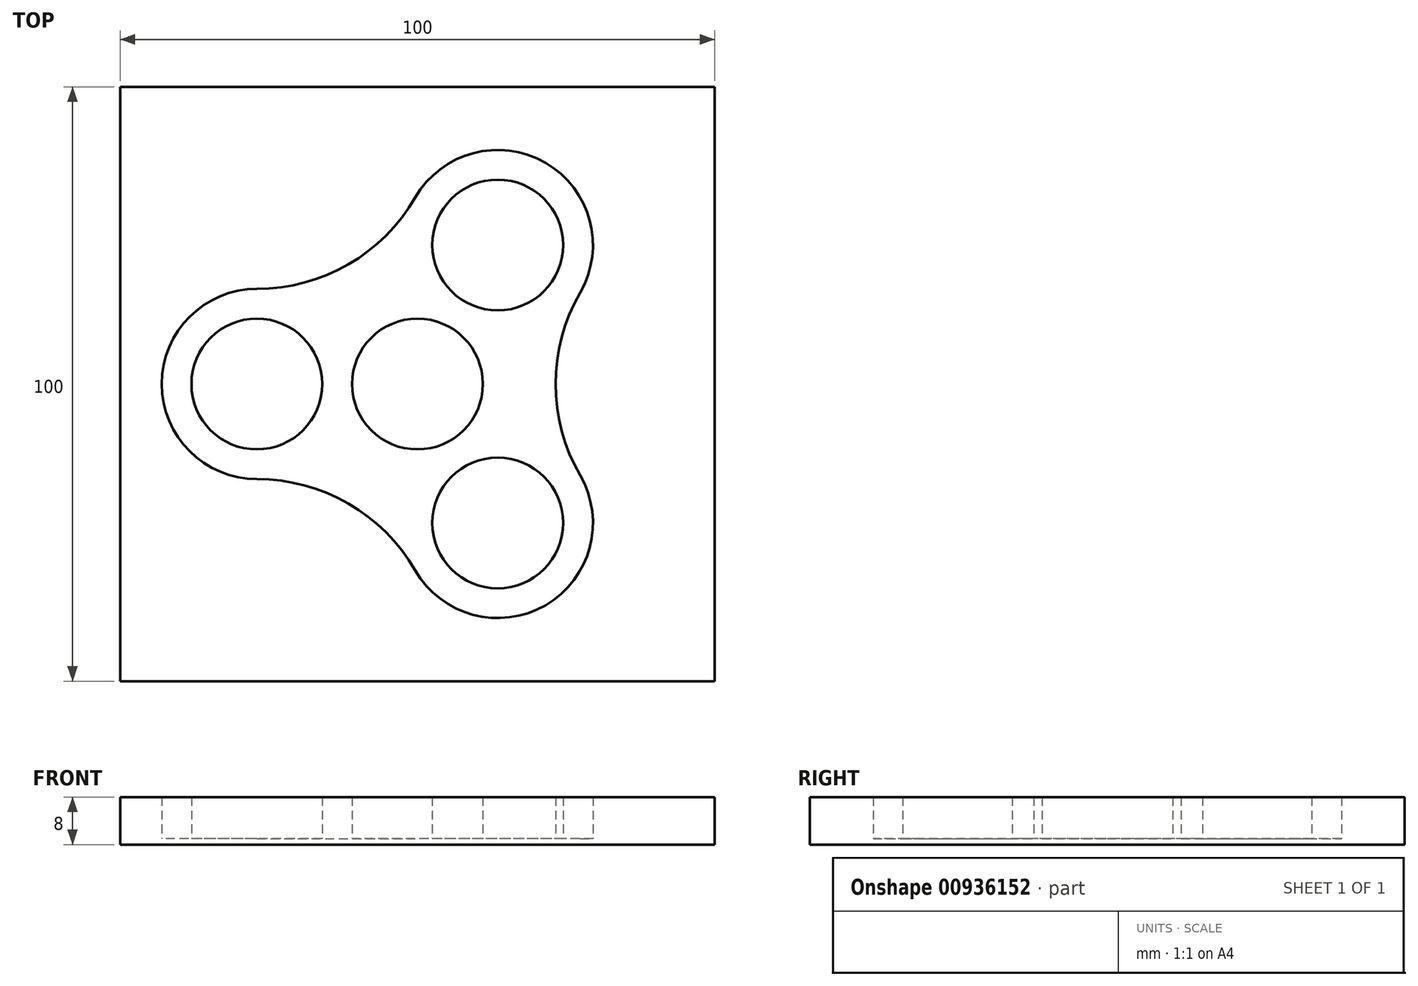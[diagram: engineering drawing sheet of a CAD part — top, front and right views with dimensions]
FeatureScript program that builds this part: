
annotation { "Feature Type Name" : "Feature", "Feature Type Description" : "" }
export const myFeature = defineFeature(function(context is Context, id is Id, definition is map)
    precondition{}
    {
        {
            var Q0;
            Q0=qCreatedBy(makeId("Top.planeOp"),FACE);
            var sketch = newSketch(context, id + "F0", { "sketchPlane" : qUnion([Q0])});
            skCircle(sketch, "E0", {"center": v(0, 0) * mm, "radius": 11 * mm});
            skCircle(sketch, "E1", {"center": v(0, 0) * mm, "radius": 16 * mm});
            skCircle(sketch, "E2", {"center": v(-27, 0) * mm, "radius": 11 * mm});
            skCircle(sketch, "E3", {"center": v(-27, 0) * mm, "radius": 16 * mm});
            skCircle(sketch, "E4.1.0", {"center": v(13.5, -23.38) * mm, "radius": 11 * mm});
            skCircle(sketch, "E4.1.1", {"center": v(13.5, -23.38) * mm, "radius": 16 * mm});
            skCircle(sketch, "E4.2.0", {"center": v(13.5, 23.38) * mm, "radius": 11 * mm});
            skCircle(sketch, "E4.2.1", {"center": v(13.5, 23.38) * mm, "radius": 16 * mm});
            skArc(sketch, "E5", {"start": v(-27, 16) * mm, "mid": v(-11.62, 20.12) * mm, "end": v(-0.36, 31.38) * mm});
            skArc(sketch, "E6.1.0", {"start": v(-0.36, -31.38) * mm, "mid": v(-11.62, -20.12) * mm, "end": v(-27, -16) * mm});
            skArc(sketch, "E6.2.0", {"start": v(27.36, 15.38) * mm, "mid": v(23.23, 0) * mm, "end": v(27.36, -15.38) * mm});
            skLineSegment(sketch, "E7.bottom", {"start": v(-50, -50) * mm, "end": v(50, -50) * mm});
            skLineSegment(sketch, "E7.top", {"start": v(-50, 50) * mm, "end": v(50, 50) * mm});
            skLineSegment(sketch, "E7.left", {"start": v(-50, -50) * mm, "end": v(-50, 50) * mm});
            skLineSegment(sketch, "E7.right", {"start": v(50, -50) * mm, "end": v(50, 50) * mm});
            skSolve(sketch);
        }
        {
            var Q0;
            {var subQ0=sQuery(id+"F0.wireOp",EDGE,"E5");Q0=makeQuery(id+"F0.imprint","IMPRINT",FACE,{"disambiguationData":[TD([[makeQuery(id+"F0.imprint","IMPRINT",EDGE,{"derivedFrom":subQ0}),1.0]])]});}
            extrude(context, id + "F1", {"entities" : qUnion([Q0]), "depth" : 7 * mm, "offsetDistance" : 25 * mm});
        }
        {
            var Q0;
            {var subQ4=sQuery(id+"F0.wireOp",EDGE,"E2");Q0=makeQuery(id+"F0.imprint","IMPRINT",FACE,{"disambiguationData":[TD([[makeQuery(id+"F0.imprint","IMPRINT",EDGE,{"derivedFrom":subQ4}),-1.0]])]});}
            var Q1;
            {var subQ4=sQuery(id+"F0.wireOp",EDGE,"E4.2.0");Q1=makeQuery(id+"F0.imprint","IMPRINT",FACE,{"disambiguationData":[TD([[makeQuery(id+"F0.imprint","IMPRINT",EDGE,{"derivedFrom":subQ4}),-1.0]])]});}
            var Q2;
            {var subQ0=sQuery(id+"F0.wireOp",EDGE,"E1");var subQ1=makeQuery(id+"F0.imprint","INTERSECT",VERTEX,{"derivedFrom":[subQ0,sQuery(id+"F0.wireOp",EDGE,"E4.2.0")]});Q2=makeQuery(id+"F0.imprint","IMPRINT",FACE,{"disambiguationData":[TD([[makeQuery(id+"F0.imprint","IMPRINT",EDGE,{"disambiguationData":[TD([[subQ1,1.0]])],"derivedFrom":subQ0}),1.0]])]});}
            var Q3;
            {var subQ0=sQuery(id+"F0.wireOp",EDGE,"E4.1.0");Q3=makeQuery(id+"F0.imprint","IMPRINT",FACE,{"disambiguationData":[TD([[makeQuery(id+"F0.imprint","IMPRINT",EDGE,{"derivedFrom":subQ0}),-1.0]])]});}
            var Q4;
            {var subQ0=sQuery(id+"F0.wireOp",EDGE,"E1");var subQ1=makeQuery(id+"F0.imprint","INTERSECT",VERTEX,{"derivedFrom":[subQ0,sQuery(id+"F0.wireOp",EDGE,"E4.1.0")]});Q4=makeQuery(id+"F0.imprint","IMPRINT",FACE,{"disambiguationData":[TD([[makeQuery(id+"F0.imprint","IMPRINT",EDGE,{"disambiguationData":[TD([[subQ1,1.0]])],"derivedFrom":subQ0}),1.0]])]});}
            var Q5;
            {var subQ5=sQuery(id+"F0.wireOp",EDGE,"E6.1.0");Q5=makeQuery(id+"F0.imprint","IMPRINT",FACE,{"disambiguationData":[TD([[makeQuery(id+"F0.imprint","IMPRINT",EDGE,{"derivedFrom":subQ5}),-1.0]])]});}
            var Q6;
            {var subQ0=sQuery(id+"F0.wireOp",EDGE,"E4.2.1");var subQ1=sQuery(id+"F0.wireOp",EDGE,"E0");var subQ2=makeQuery(id+"F0.imprint","INTERSECT",VERTEX,{"derivedFrom":[subQ1,subQ0]});Q6=makeQuery(id+"F0.imprint","IMPRINT",FACE,{"disambiguationData":[TD([[makeQuery(id+"F0.imprint","IMPRINT",EDGE,{"disambiguationData":[TD([[subQ2,1.0]])],"derivedFrom":subQ1}),-1.0]])]});}
            var Q7;
            {var subQ0=sQuery(id+"F0.wireOp",EDGE,"E3");var subQ1=sQuery(id+"F0.wireOp",EDGE,"E0");var subQ2=makeQuery(id+"F0.imprint","INTERSECT",VERTEX,{"derivedFrom":[subQ1,subQ0]});Q7=makeQuery(id+"F0.imprint","IMPRINT",FACE,{"disambiguationData":[TD([[makeQuery(id+"F0.imprint","IMPRINT",EDGE,{"disambiguationData":[TD([[subQ2,-1.0]])],"derivedFrom":subQ1}),-1.0]])]});}
            var Q8;
            {var subQ0=sQuery(id+"F0.wireOp",EDGE,"E1");var subQ1=makeQuery(id+"F0.imprint","INTERSECT",VERTEX,{"derivedFrom":[subQ0,sQuery(id+"F0.wireOp",EDGE,"E2")]});Q8=makeQuery(id+"F0.imprint","IMPRINT",FACE,{"disambiguationData":[TD([[makeQuery(id+"F0.imprint","IMPRINT",EDGE,{"disambiguationData":[TD([[subQ1,1.0]])],"derivedFrom":subQ0}),1.0]])]});}
            var Q9;
            {var subQ0=sQuery(id+"F0.wireOp",EDGE,"E3");var subQ1=sQuery(id+"F0.wireOp",EDGE,"E0");var subQ2=makeQuery(id+"F0.imprint","INTERSECT",VERTEX,{"derivedFrom":[subQ1,subQ0]});Q9=makeQuery(id+"F0.imprint","IMPRINT",FACE,{"disambiguationData":[TD([[makeQuery(id+"F0.imprint","IMPRINT",EDGE,{"disambiguationData":[TD([[subQ2,1.0]])],"derivedFrom":subQ1}),-1.0]])]});}
            var Q10;
            {var subQ5=sQuery(id+"F0.wireOp",EDGE,"E5");Q10=makeQuery(id+"F0.imprint","IMPRINT",FACE,{"disambiguationData":[TD([[makeQuery(id+"F0.imprint","IMPRINT",EDGE,{"derivedFrom":subQ5}),-1.0]])]});}
            var Q11;
            {var subQ5=sQuery(id+"F0.wireOp",EDGE,"E6.2.0");Q11=makeQuery(id+"F0.imprint","IMPRINT",FACE,{"disambiguationData":[TD([[makeQuery(id+"F0.imprint","IMPRINT",EDGE,{"derivedFrom":subQ5}),-1.0]])]});}
            extrude(context, id + "F2", {"entities" : qUnion([Q0, Q1, Q2, Q3, Q4, Q5, Q6, Q7, Q8, Q9, Q10, Q11]), "depth" : 7 * mm, "offsetDistance" : 25 * mm});
        }
        {
            var Q0;
            Q0=makeQuery(id+"F2.opExtrude","CAP_EDGE",EDGE,{"disambiguationData":[OSD([sQuery(id+"F0.wireOp",EDGE,"E4.2.1")])],"isStart":false});
            var Q1;
            Q1=makeQuery(id+"F2.opExtrude","CAP_EDGE",EDGE,{"disambiguationData":[OSD([sQuery(id+"F0.wireOp",EDGE,"E4.2.1")])],"isStart":true});
            fillet(context, id + "F3", {"entities" : qUnion([Q0, Q1]), "radius" : 3.5 * mm, "tangentPropagation" : true, "allowEdgeOverflow" : false});
        }
        {
            var Q0;
            Q0=makeQuery(id+"F2.opExtrude","SWEPT_BODY",BODY,{"disambiguationData":[OSD([sQuery(id+"F0.wireOp",EDGE,"E0"),sQuery(id+"F0.wireOp",EDGE,"E2"),sQuery(id+"F0.wireOp",EDGE,"E3"),sQuery(id+"F0.wireOp",EDGE,"E4.1.0"),sQuery(id+"F0.wireOp",EDGE,"E4.1.1"),sQuery(id+"F0.wireOp",EDGE,"E4.2.0"),sQuery(id+"F0.wireOp",EDGE,"E4.2.1"),sQuery(id+"F0.wireOp",EDGE,"E5"),sQuery(id+"F0.wireOp",EDGE,"E6.1.0"),sQuery(id+"F0.wireOp",EDGE,"E6.2.0")])]});
            var Q1;
            Q1=makeQuery(id+"F1.opExtrude","SWEPT_BODY",BODY,{"disambiguationData":[OSD([sQuery(id+"F0.wireOp",EDGE,"E3"),sQuery(id+"F0.wireOp",EDGE,"E4.1.1"),sQuery(id+"F0.wireOp",EDGE,"E4.2.1"),sQuery(id+"F0.wireOp",EDGE,"E5"),sQuery(id+"F0.wireOp",EDGE,"E6.1.0"),sQuery(id+"F0.wireOp",EDGE,"E6.2.0"),sQuery(id+"F0.wireOp",EDGE,"E7.bottom"),sQuery(id+"F0.wireOp",EDGE,"E7.top"),sQuery(id+"F0.wireOp",EDGE,"E7.left"),sQuery(id+"F0.wireOp",EDGE,"E7.right")])]});
            booleanBodies(context, id + "F4", {"operationType" : BooleanOperationType.SUBTRACTION, "tools" : qUnion([Q0]), "targets" : qUnion([Q1])});
        }
        {
            var Q0;
            Q0=qCreatedBy(makeId("Top.planeOp"),FACE);
            var sketch = newSketch(context, id + "F5", { "sketchPlane" : qUnion([Q0])});
            skLineSegment(sketch, "E8", {"start": v(-50, 50) * mm, "end": v(-50, -50) * mm});
            skLineSegment(sketch, "E9", {"start": v(-50, -50) * mm, "end": v(50, -50) * mm});
            skLineSegment(sketch, "E10", {"start": v(50, -50) * mm, "end": v(50, 50) * mm});
            skLineSegment(sketch, "E11", {"start": v(50, 50) * mm, "end": v(-50, 50) * mm});
            skSolve(sketch);
        }
        {
            var Q0;
            Q0 = qSketchRegion(id + "F5", true);
            extrude(context, id + "F6", {"entities" : qUnion([Q0]), "operationType" : NewBodyOperationType.ADD, "oppositeDirection" : true, "depth" : 1 * mm, "offsetDistance" : 25 * mm});
        }
        {
            var Q0;
            Q0=makeQuery(id+"F6.opExtrude","CAP_FACE",FACE,{"disambiguationData":[OSD([sQuery(id+"F5.wireOp",EDGE,"E8"),sQuery(id+"F5.wireOp",EDGE,"E9"),sQuery(id+"F5.wireOp",EDGE,"E10"),sQuery(id+"F5.wireOp",EDGE,"E11")])],"isStart":true});
            var sketch = newSketch(context, id + "F7", { "sketchPlane" : qUnion([Q0])});
            skCircle(sketch, "E12", {"center": v(0, 0) * mm, "radius": 11 * mm});
            skCircle(sketch, "E13", {"center": v(13.5, 23.38) * mm, "radius": 11 * mm});
            skCircle(sketch, "E14", {"center": v(-27, 0) * mm, "radius": 11 * mm});
            skCircle(sketch, "E15", {"center": v(13.5, -23.38) * mm, "radius": 11 * mm});
            skSolve(sketch);
        }
        {
            var Q0;
            Q0 = qSketchRegion(id + "F7", true);
            extrude(context, id + "F8", {"entities" : qUnion([Q0]), "operationType" : NewBodyOperationType.ADD, "depth" : 7 * mm, "offsetDistance" : 25 * mm});
        }
    });
